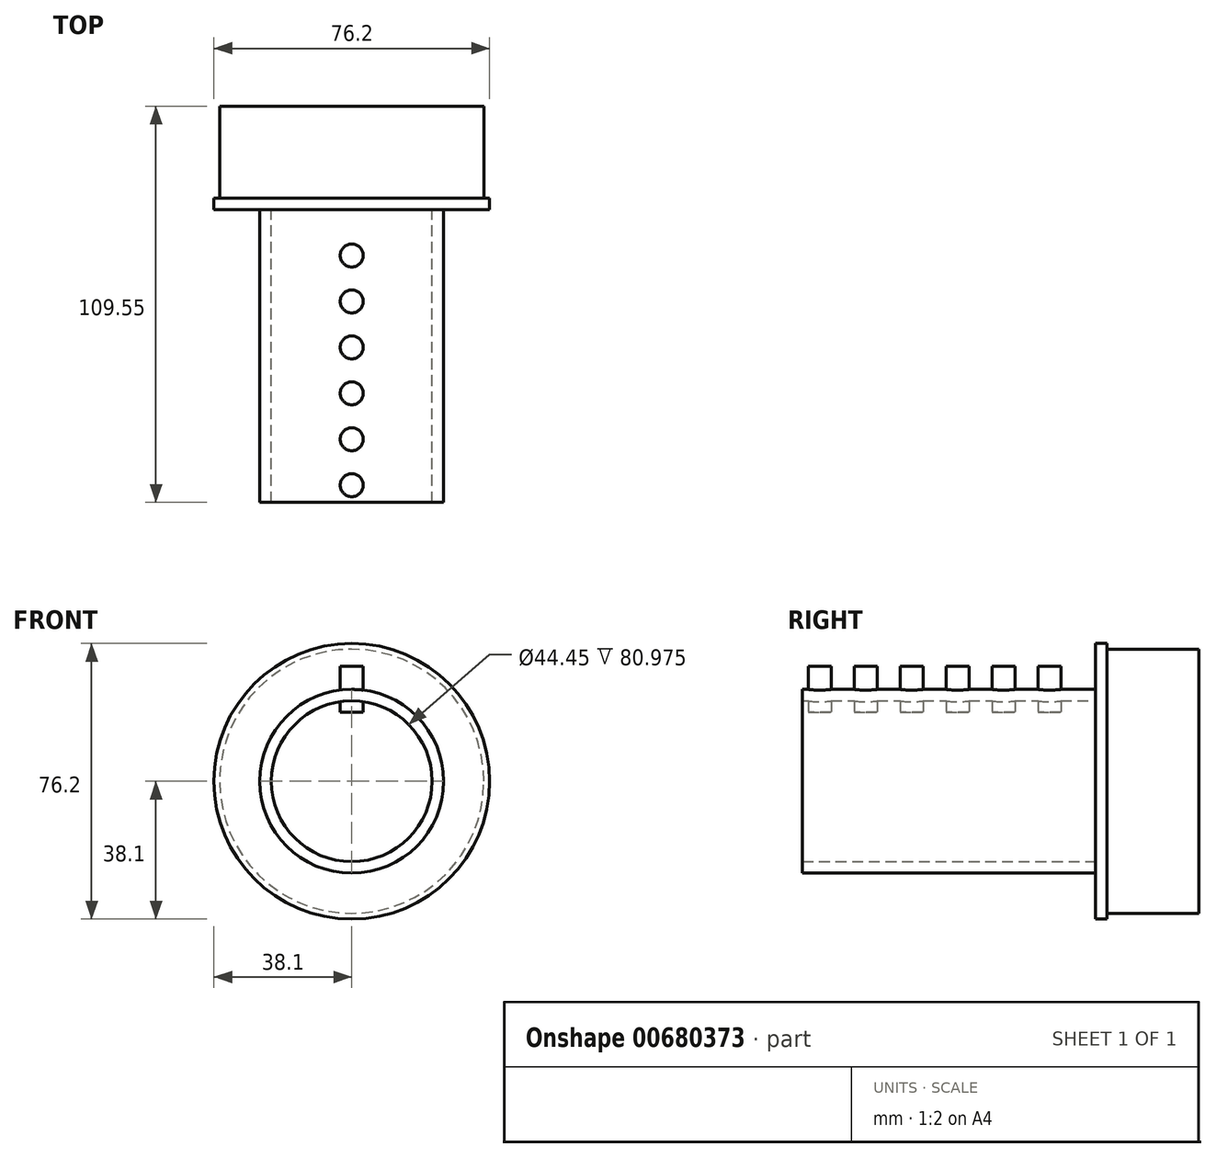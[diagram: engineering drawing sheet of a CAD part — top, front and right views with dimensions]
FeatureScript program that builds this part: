
annotation { "Feature Type Name" : "Feature", "Feature Type Description" : "" }
export const myFeature = defineFeature(function(context is Context, id is Id, definition is map)
    precondition{}
    {
        {
            var Q0;
            Q0=qCreatedBy(makeId("Front.planeOp"),FACE);
            var sketch = newSketch(context, id + "F0", { "sketchPlane" : qUnion([Q0])});
            skCircle(sketch, "E0", {"center": v(0, 0) * mm, "radius": 22.22 * mm});
            skCircle(sketch, "E1", {"center": v(0, 0) * mm, "radius": 25.4 * mm});
            skSolve(sketch);
        }
        {
            var Q0;
            Q0=qSketchRegion(id+"F0",true);
            extrude(context, id + "F1", {"entities" : qUnion([Q0]), "depth" : 84.15 * mm, "offsetDistance" : 25.4 * mm});
        }
        {
            var Q0;
            Q0=qCreatedBy(makeId("Front.planeOp"),FACE);
            var sketch = newSketch(context, id + "F2", { "sketchPlane" : qUnion([Q0])});
            skCircle(sketch, "E2", {"center": v(0, 0) * mm, "radius": 38.1 * mm});
            skSolve(sketch);
        }
        {
            var Q0;
            Q0=qSketchRegion(id+"F2",true);
            extrude(context, id + "F3", {"entities" : qUnion([Q0]), "operationType" : NewBodyOperationType.ADD, "depth" : 3.17 * mm, "offsetDistance" : 25.4 * mm});
        }
        {
            var Q0;
            Q0=makeQuery(id+"F3.boolean.opBoolean","MERGE",FACE,{"derivedFrom":[makeQuery(id+"F1.opExtrude","CAP_FACE",FACE,{"disambiguationData":[OSD([sQuery(id+"F0.wireOp",EDGE,"2ZOCY7LP-zA3b-KTJU-QNer-IYBKqWAxzzcB"),sQuery(id+"F0.wireOp",EDGE,"u1ooH0wt-ulDo-FeRP-52ZV-qPab0OzWQUdP"),sQuery(id+"F0.wireOp",EDGE,"mvX2gNnv-Yt3d-CT5T-wEDv-7d7Wdy3MzFJP"),sQuery(id+"F0.wireOp",EDGE,"TDgHw8LF-Ugaz-y4qZ-vyZB-lc77xSGdSNCC")])],"isStart":true}),makeQuery(id+"F3.opExtrude","CAP_FACE",FACE,{"disambiguationData":[OSD([sQuery(id+"F2.wireOp",EDGE,"E2")])],"isStart":true})]});
            var sketch = newSketch(context, id + "F4", { "sketchPlane" : qUnion([Q0])});
            skCircle(sketch, "E3", {"center": v(0, 0) * mm, "radius": 36.51 * mm});
            skSolve(sketch);
        }
        {
            var Q0;
            Q0=qSketchRegion(id+"F4",true);
            extrude(context, id + "F5", {"entities" : qUnion([Q0]), "operationType" : NewBodyOperationType.ADD, "depth" : 25.4 * mm, "offsetDistance" : 25.4 * mm});
        }
        {
            var Q0;
            Q0=qCreatedBy(makeId("Top.planeOp"),FACE);
            cPlane(context, id + "F6", {"entities" : qUnion([Q0]), "cplaneType" : CPlaneType.OFFSET, "offset" : 19.05 * mm, "width" : 152.4 * mm, "height" : 152.4 * mm});
        }
        {
            var Q0;
            Q0=qCreatedBy(id+"F6.planeOp",FACE);
            var sketch = newSketch(context, id + "F7", { "sketchPlane" : qUnion([Q0])});
            skCircle(sketch, "E4", {"center": v(0, -15.88) * mm, "radius": 3.18 * mm});
            skCircle(sketch, "E5.0.1.0", {"center": v(0, -28.58) * mm, "radius": 3.18 * mm});
            skCircle(sketch, "E5.0.2.0", {"center": v(0, -41.28) * mm, "radius": 3.18 * mm});
            skCircle(sketch, "E5.0.3.0", {"center": v(0, -53.98) * mm, "radius": 3.18 * mm});
            skCircle(sketch, "E5.0.4.0", {"center": v(0, -66.68) * mm, "radius": 3.18 * mm});
            skCircle(sketch, "E5.0.5.0", {"center": v(0, -79.38) * mm, "radius": 3.18 * mm});
            skLineSegment(sketch, "E5.direction1", {"start": v(0, -15.88) * mm, "end": v(25.4, -15.88) * mm, "construction": true});
            skLineSegment(sketch, "E5.direction2", {"start": v(0, -15.88) * mm, "end": v(0, -28.58) * mm, "construction": true});
            skSolve(sketch);
        }
        {
            var Q0;
            Q0 = qSketchRegion(id + "F7", true);
            extrude(context, id + "F8", {"entities" : qUnion([Q0]), "operationType" : NewBodyOperationType.ADD, "depth" : 12.7 * mm, "offsetDistance" : 25.4 * mm});
        }
    });
